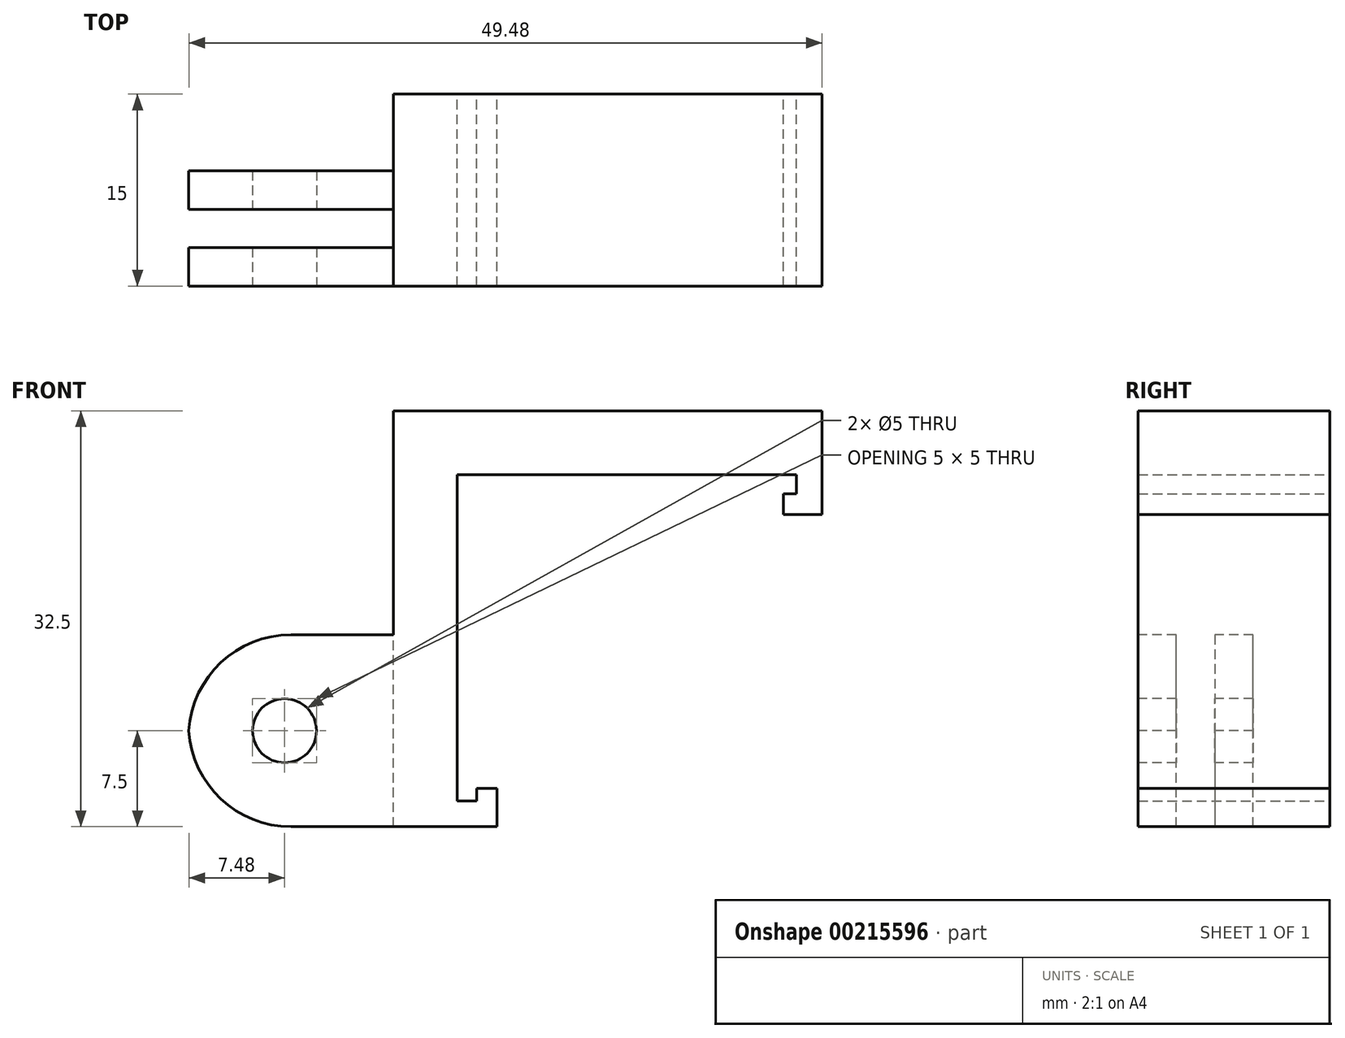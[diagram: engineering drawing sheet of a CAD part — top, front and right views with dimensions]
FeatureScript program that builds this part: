
annotation { "Feature Type Name" : "Feature", "Feature Type Description" : "" }
export const myFeature = defineFeature(function(context is Context, id is Id, definition is map)
    precondition{}
    {
        {
            var Q0;
            Q0=qCreatedBy(makeId("Front.planeOp"),FACE);
            var sketch = newSketch(context, id + "F0", { "sketchPlane" : qUnion([Q0])});
            skLineSegment(sketch, "E0", {"start": v(0, 0) * mm, "end": v(25, 0) * mm});
            skLineSegment(sketch, "E1", {"start": v(0, 0) * mm, "end": v(0, -23.59) * mm});
            skLineSegment(sketch, "E2", {"start": v(-5, -24) * mm, "end": v(-5, 5) * mm});
            skLineSegment(sketch, "E3", {"start": v(-5, 5) * mm, "end": v(25, 5) * mm});
            skLineSegment(sketch, "E4", {"start": v(-5, -24) * mm, "end": v(-5, -25.5) * mm});
            skLineSegment(sketch, "E5", {"start": v(0, -23.59) * mm, "end": v(0, -25.09) * mm});
            skLineSegment(sketch, "E6", {"start": v(0, -25.5) * mm, "end": v(0, -25.09) * mm});
            skLineSegment(sketch, "E7", {"start": v(0, -25.5) * mm, "end": v(1.5, -25.5) * mm});
            skLineSegment(sketch, "E8", {"start": v(1.5, -24.5) * mm, "end": v(1.5, -25.5) * mm});
            skLineSegment(sketch, "E9", {"start": v(1.5, -24.5) * mm, "end": v(3.1, -24.5) * mm});
            skLineSegment(sketch, "E10", {"start": v(25, 0) * mm, "end": v(26.5, 0) * mm});
            skLineSegment(sketch, "E11", {"start": v(26.5, 0) * mm, "end": v(26.5, -1.5) * mm});
            skLineSegment(sketch, "E12", {"start": v(26.5, -1.5) * mm, "end": v(25.5, -1.5) * mm});
            skLineSegment(sketch, "E13", {"start": v(25.5, -1.5) * mm, "end": v(25.5, -3.1) * mm});
            skPoint(sketch, "E14", {"position": v(0, -27.5) * mm});
            skLineSegment(sketch, "E15", {"start": v(-5, -25.5) * mm, "end": v(-5, -27.5) * mm});
            skLineSegment(sketch, "E16", {"start": v(-5, -27.5) * mm, "end": v(0, -27.5) * mm});
            skLineSegment(sketch, "E17", {"start": v(3.1, -24.5) * mm, "end": v(3.1, -27.5) * mm});
            skLineSegment(sketch, "E18", {"start": v(3.1, -27.5) * mm, "end": v(0, -27.5) * mm});
            skLineSegment(sketch, "E19", {"start": v(25.5, -3.1) * mm, "end": v(28.5, -3.1) * mm});
            skLineSegment(sketch, "E20", {"start": v(28.5, -3.1) * mm, "end": v(28.5, 5) * mm});
            skLineSegment(sketch, "E21", {"start": v(28.5, 5) * mm, "end": v(25, 5) * mm});
            skSolve(sketch);
        }
        {
            var Q0;
            Q0 = qSketchRegion(id + "F0", true);
            extrude(context, id + "F1", {"entities" : qUnion([Q0]), "depth" : 15 * mm});
        }
        {
            var Q0;
            Q0=makeQuery(id+"F1.opExtrude","SWEPT_FACE",FACE,{"disambiguationData":[OSD([sQuery(id+"F0.wireOp",EDGE,"E2"),sQuery(id+"F0.wireOp",EDGE,"E4"),sQuery(id+"F0.wireOp",EDGE,"E15")])]});
            var sketch = newSketch(context, id + "F2", { "sketchPlane" : qUnion([Q0])});
            skLineSegment(sketch, "E22", {"start": v(0, -27.5) * mm, "end": v(0, -12.5) * mm});
            skLineSegment(sketch, "E23", {"start": v(0, -12.5) * mm, "end": v(15, -12.5) * mm});
            skPoint(sketch, "E24", {"position": v(12, -12.5) * mm});
            skPoint(sketch, "E25", {"position": v(9, -12.5) * mm});
            skPoint(sketch, "E26", {"position": v(3, -12.5) * mm});
            skPoint(sketch, "E27", {"position": v(6, -12.5) * mm});
            skLineSegment(sketch, "E28", {"start": v(3, -12.5) * mm, "end": v(3, -27.5) * mm});
            skLineSegment(sketch, "E29", {"start": v(3, -27.5) * mm, "end": v(6, -27.5) * mm});
            skLineSegment(sketch, "E30", {"start": v(6, -27.5) * mm, "end": v(6, -12.5) * mm});
            skLineSegment(sketch, "E31", {"start": v(9, -12.5) * mm, "end": v(9, -27.5) * mm});
            skLineSegment(sketch, "E32", {"start": v(9, -27.5) * mm, "end": v(12, -27.5) * mm});
            skLineSegment(sketch, "E33", {"start": v(12, -27.5) * mm, "end": v(12, -12.5) * mm});
            skSolve(sketch);
        }
        {
            var Q0;
            {var subQ0=sQuery(id+"F2.wireOp",EDGE,"E22");Q0=makeQuery(id+"F2.imprint","IMPRINT",FACE,{"disambiguationData":[TD([[makeQuery(id+"F2.imprint","IMPRINT",EDGE,{"derivedFrom":subQ0}),1.0]])]});}
            var Q1;
            {var subQ0=sQuery(id+"F2.wireOp",EDGE,"E30");Q1=makeQuery(id+"F2.imprint","IMPRINT",FACE,{"disambiguationData":[TD([[makeQuery(id+"F2.imprint","IMPRINT",EDGE,{"derivedFrom":subQ0}),-1.0]])]});}
            var Q2;
            {var subQ4=sQuery(id+"F2.wireOp",EDGE,"E33");Q2=makeQuery(id+"F2.imprint","IMPRINT",FACE,{"disambiguationData":[TD([[makeQuery(id+"F2.imprint","IMPRINT",EDGE,{"derivedFrom":subQ4}),-1.0]])]});}
            extrude(context, id + "F3", {"entities" : qUnion([Q0, Q1, Q2]), "operationType" : NewBodyOperationType.ADD, "depth" : 16 * mm});
        }
        {
            var Q0;
            {var subQ0=sQuery(id+"F0.wireOp",EDGE,"E15");var subQ1=sQuery(id+"F0.wireOp",EDGE,"E4");var subQ2=sQuery(id+"F0.wireOp",EDGE,"E2");Q0=makeQuery(id+"F3.boolean.opBoolean","MERGE",FACE,{"derivedFrom":[makeQuery(id+"F1.opExtrude","CAP_FACE",FACE,{"disambiguationData":[OSD([sQuery(id+"F0.wireOp",EDGE,"E0"),sQuery(id+"F0.wireOp",EDGE,"E1"),subQ2,sQuery(id+"F0.wireOp",EDGE,"E3"),subQ1,sQuery(id+"F0.wireOp",EDGE,"E5"),sQuery(id+"F0.wireOp",EDGE,"E6"),sQuery(id+"F0.wireOp",EDGE,"E7"),sQuery(id+"F0.wireOp",EDGE,"E8"),sQuery(id+"F0.wireOp",EDGE,"E9"),sQuery(id+"F0.wireOp",EDGE,"E10"),sQuery(id+"F0.wireOp",EDGE,"E11"),sQuery(id+"F0.wireOp",EDGE,"E12"),sQuery(id+"F0.wireOp",EDGE,"E13"),subQ0,sQuery(id+"F0.wireOp",EDGE,"E16"),sQuery(id+"F0.wireOp",EDGE,"E17"),sQuery(id+"F0.wireOp",EDGE,"E18"),sQuery(id+"F0.wireOp",EDGE,"E19"),sQuery(id+"F0.wireOp",EDGE,"E20"),sQuery(id+"F0.wireOp",EDGE,"E21")])],"isStart":false}),makeQuery(id+"F3.opExtrude","SWEPT_FACE",FACE,{"disambiguationData":[OSD([subQ2,subQ1,subQ0])]})]});}
            var sketch = newSketch(context, id + "F4", { "sketchPlane" : qUnion([Q0])});
            skLineSegment(sketch, "E34", {"start": v(-21, -20) * mm, "end": v(-16, -20) * mm});
            skLineSegment(sketch, "E35", {"start": v(-16, -20) * mm, "end": v(-13.5, -20) * mm});
            skCircle(sketch, "E36", {"center": v(-13.5, -20) * mm, "radius": 2.5 * mm});
            skSolve(sketch);
        }
        {
            var Q0;
            Q0 = qSketchRegion(id + "F4", true);
            extrude(context, id + "F5", {"entities" : qUnion([Q0]), "operationType" : NewBodyOperationType.REMOVE, "oppositeDirection" : true, "depth" : 25 * mm});
        }
        {
            var Q0;
            {var subQ0=sQuery(id+"F2.wireOp",EDGE,"E23");Q0=makeQuery(id+"F3.opExtrude","CAP_EDGE",EDGE,{"disambiguationData":[OSD([subQ0]),TDD([makeQuery(id+"F2.imprint","IMPRINT",EDGE,{"disambiguationData":[TD([[makeQuery(id+"F2.imprint","INTERSECT",VERTEX,{"derivedFrom":[subQ0,sQuery(id+"F2.wireOp",EDGE,"E33")]}),-1.0]])],"derivedFrom":subQ0})])],"isStart":false});}
            var Q1;
            {var subQ0=sQuery(id+"F2.wireOp",EDGE,"E23");Q1=makeQuery(id+"F3.opExtrude","CAP_EDGE",EDGE,{"disambiguationData":[OSD([subQ0]),TDD([makeQuery(id+"F2.imprint","IMPRINT",EDGE,{"disambiguationData":[TD([[makeQuery(id+"F2.imprint","INTERSECT",VERTEX,{"derivedFrom":[subQ0,sQuery(id+"F2.wireOp",EDGE,"E30")]}),-1.0]])],"derivedFrom":subQ0})])],"isStart":false});}
            var Q2;
            {var subQ0=sQuery(id+"F2.wireOp",EDGE,"E23");Q2=makeQuery(id+"F3.opExtrude","CAP_EDGE",EDGE,{"disambiguationData":[OSD([subQ0]),TDD([makeQuery(id+"F2.imprint","IMPRINT",EDGE,{"disambiguationData":[TD([[makeQuery(id+"F2.imprint","INTERSECT",VERTEX,{"derivedFrom":[subQ0,sQuery(id+"F2.wireOp",EDGE,"E28")]}),1.0]])],"derivedFrom":subQ0})])],"isStart":false});}
            var Q3;
            {var subQ0=sQuery(id+"F0.wireOp",EDGE,"E16");var subQ1=sQuery(id+"F0.wireOp",EDGE,"E15");var subQ2=makeQuery(id+"F1.opExtrude","SWEPT_EDGE",EDGE,{"disambiguationData":[OSD([subQ1,subQ0])]});Q3=makeQuery(id+"F3.opExtrude","CAP_EDGE",EDGE,{"disambiguationData":[OSD([subQ1,subQ0]),TDD([makeQuery(id+"F2.imprint","IMPRINT",EDGE,{"disambiguationData":[TD([[makeQuery(id+"F2.imprint","INTERSECT",VERTEX,{"derivedFrom":[subQ2,sQuery(id+"F2.wireOp",EDGE,"E22")]}),1.0]])],"derivedFrom":subQ2})])],"isStart":false});}
            var Q4;
            {var subQ0=sQuery(id+"F0.wireOp",EDGE,"E16");var subQ1=sQuery(id+"F0.wireOp",EDGE,"E15");var subQ2=makeQuery(id+"F1.opExtrude","SWEPT_EDGE",EDGE,{"disambiguationData":[OSD([subQ1,subQ0])]});Q4=makeQuery(id+"F3.opExtrude","CAP_EDGE",EDGE,{"disambiguationData":[OSD([subQ1,subQ0]),TDD([makeQuery(id+"F2.imprint","IMPRINT",EDGE,{"disambiguationData":[TD([[makeQuery(id+"F2.imprint","INTERSECT",VERTEX,{"derivedFrom":[subQ2,sQuery(id+"F2.wireOp",EDGE,"E29"),sQuery(id+"F2.wireOp",EDGE,"E30")]}),1.0]])],"derivedFrom":subQ2})])],"isStart":false});}
            var Q5;
            {var subQ0=sQuery(id+"F0.wireOp",EDGE,"E15");var subQ1=sQuery(id+"F0.wireOp",EDGE,"E16");var subQ2=makeQuery(id+"F1.opExtrude","SWEPT_EDGE",EDGE,{"disambiguationData":[OSD([subQ0,subQ1])]});Q5=makeQuery(id+"F3.opExtrude","CAP_EDGE",EDGE,{"disambiguationData":[OSD([subQ0,subQ1]),TDD([makeQuery(id+"F2.imprint","IMPRINT",EDGE,{"disambiguationData":[TD([[makeQuery(id+"F2.imprint","INTERSECT",VERTEX,{"derivedFrom":[subQ2,sQuery(id+"F2.wireOp",EDGE,"E32"),sQuery(id+"F2.wireOp",EDGE,"E33")]}),1.0]])],"derivedFrom":subQ2})])],"isStart":false});}
            fillet(context, id + "F6", {"entities" : qUnion([Q0, Q1, Q2, Q3, Q4, Q5]), "radius" : 8 * mm, "tangentPropagation" : true, "allowEdgeOverflow" : false});
        }
    });
